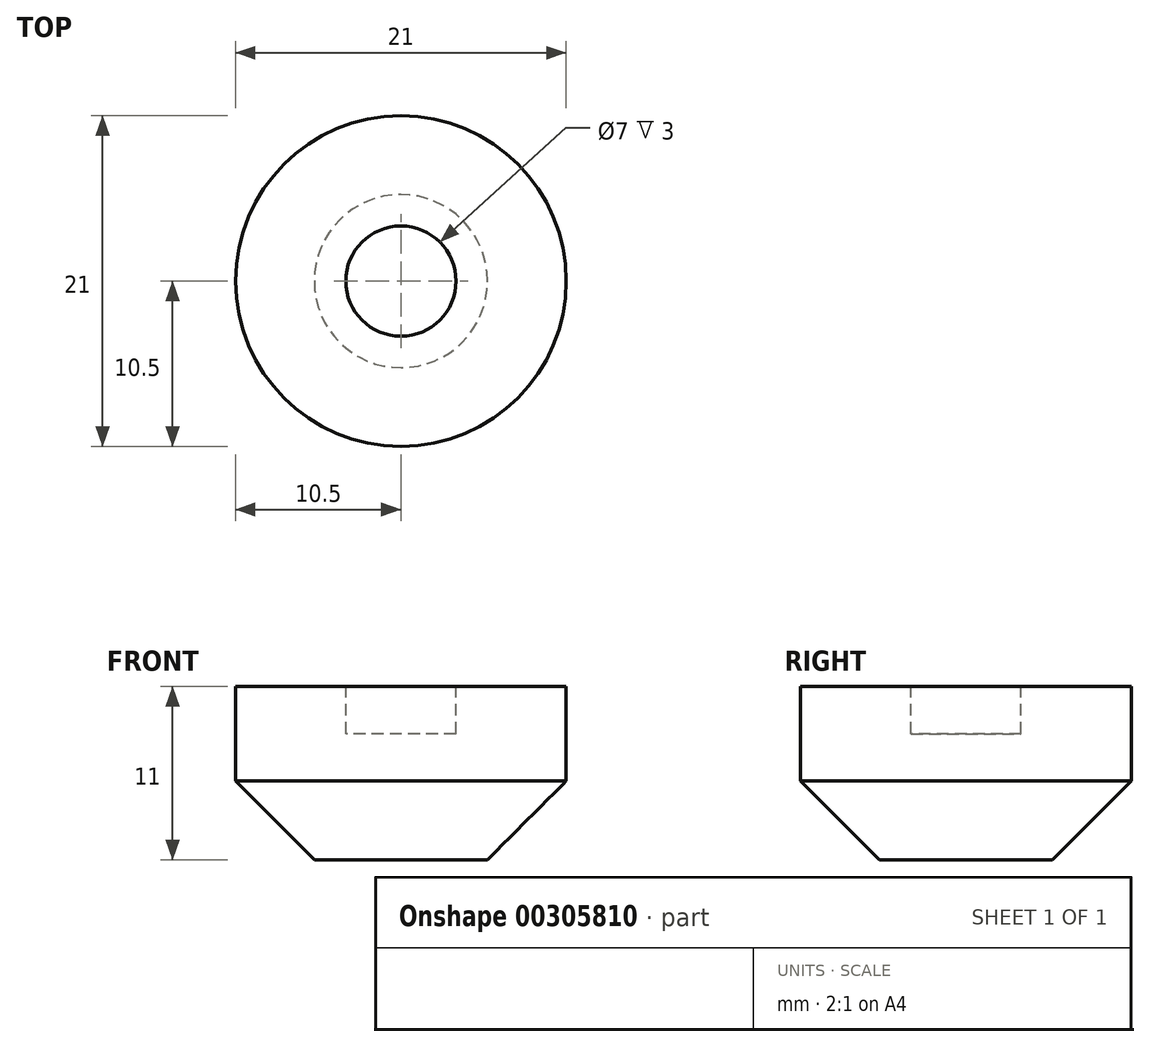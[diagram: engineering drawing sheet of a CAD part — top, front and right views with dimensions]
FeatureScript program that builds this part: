
annotation { "Feature Type Name" : "Feature", "Feature Type Description" : "" }
export const myFeature = defineFeature(function(context is Context, id is Id, definition is map)
    precondition{}
    {
        {
            var Q0;
            Q0=qCreatedBy(makeId("Top.planeOp"),FACE);
            var sketch = newSketch(context, id + "F0", { "sketchPlane" : qUnion([Q0])});
            skCircle(sketch, "E0", {"center": v(0, 0) * mm, "radius": 10.5 * mm});
            skSolve(sketch);
        }
        {
            var Q0;
            Q0 = qSketchRegion(id + "F0", true);
            extrude(context, id + "F1", {"entities" : qUnion([Q0]), "depth" : 11 * mm});
        }
        {
            var Q0;
            Q0=makeQuery(id+"F1.opExtrude","CAP_FACE",FACE,{"disambiguationData":[OSD([sQuery(id+"F0.wireOp",EDGE,"E0")])],"isStart":false});
            var sketch = newSketch(context, id + "F2", { "sketchPlane" : qUnion([Q0])});
            skCircle(sketch, "E1", {"center": v(0, 0) * mm, "radius": 3.5 * mm});
            skSolve(sketch);
        }
        {
            var Q0;
            Q0 = qSketchRegion(id + "F2", true);
            extrude(context, id + "F3", {"entities" : qUnion([Q0]), "operationType" : NewBodyOperationType.REMOVE, "oppositeDirection" : true, "depth" : 3 * mm});
        }
        {
            var Q0;
            Q0=makeQuery(id+"F1.opExtrude","CAP_EDGE",EDGE,{"disambiguationData":[OSD([sQuery(id+"F0.wireOp",EDGE,"E0")])],"isStart":true});
            chamfer(context, id + "F4", {"entities" : qUnion([Q0]), "width" : 5 * mm, "tangentPropagation" : true});
        }
    });
